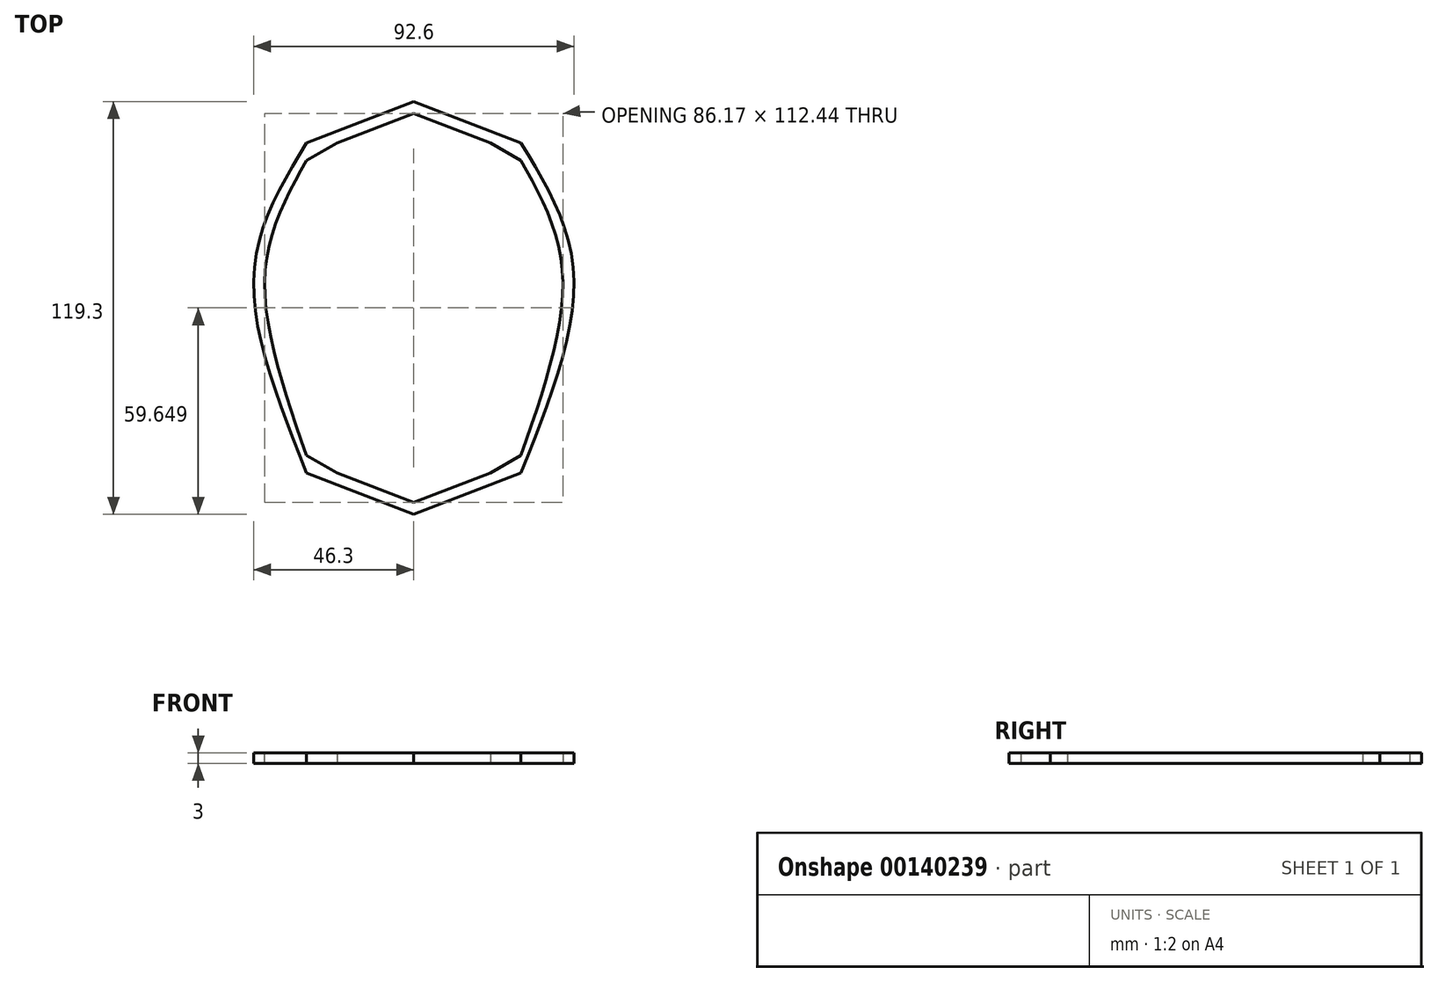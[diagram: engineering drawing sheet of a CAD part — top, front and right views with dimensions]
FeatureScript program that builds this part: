
annotation { "Feature Type Name" : "Feature", "Feature Type Description" : "" }
export const myFeature = defineFeature(function(context is Context, id is Id, definition is map)
    precondition{}
    {
        {
            var Q0;
            Q0=qCreatedBy(makeId("Top.planeOp"),FACE);
            var sketch = newSketch(context, id + "F0", { "sketchPlane" : qUnion([Q0])});
            skLineSegment(sketch, "E0", {"start": v(0, 37.5) * mm, "end": v(0, 49.5) * mm, "construction": true});
            skLineSegment(sketch, "E1", {"start": v(-31, 37.5) * mm, "end": v(0, 49.5) * mm});
            skLineSegment(sketch, "E2", {"start": v(0, 49.5) * mm, "end": v(31, 37.5) * mm});
            skLineSegment(sketch, "E3", {"start": v(0, 49.5) * mm, "end": v(0, 46.3) * mm, "construction": true});
            skLineSegment(sketch, "E4", {"start": v(0, 46.07) * mm, "end": v(-22.14, 37.5) * mm, "construction": true});
            skLineSegment(sketch, "E5.MirrorCS", {"start": v(0, 46.07) * mm, "end": v(22.14, 37.5) * mm, "construction": true});
            skLineSegment(sketch, "E6", {"start": v(0, 46.07) * mm, "end": v(22.14, 37.5) * mm});
            skLineSegment(sketch, "E7", {"start": v(0, 46.07) * mm, "end": v(-22.14, 37.5) * mm});
            skLineSegment(sketch, "E8", {"start": v(-43, 0) * mm, "end": v(-46.2, 0) * mm, "construction": true});
            skLineSegment(sketch, "E9", {"start": v(43, 0) * mm, "end": v(46.2, 0) * mm, "construction": true});
            skLineSegment(sketch, "E10", {"start": v(0, -28.4) * mm, "end": v(0, -57.8) * mm, "construction": true});
            skFitSpline(sketch, "E11", {"points": [v(-31, 37.5) * mm, v(-46.2, 0) * mm, v(-31, -57.8) * mm], "startDerivative": vector(-47.53, -78.05) * mm, "endDerivative": vector(44.54, -111.47) * mm});
            skFitSpline(sketch, "E12", {"points": [v(-31, 32.5) * mm, v(-43, 0) * mm, v(-31, -52.8) * mm], "startDerivative": vector(-37.8, -68.26) * mm, "endDerivative": vector(35.1, -101.12) * mm});
            skLineSegment(sketch, "E13", {"start": v(0, -57.8) * mm, "end": v(0, -69.8) * mm, "construction": true});
            skLineSegment(sketch, "E14", {"start": v(0, -69.8) * mm, "end": v(0, -66.37) * mm, "construction": true});
            skLineSegment(sketch, "E15", {"start": v(-22.14, -57.8) * mm, "end": v(0, -66.37) * mm});
            skLineSegment(sketch, "E16", {"start": v(0, -66.37) * mm, "end": v(22.14, -57.8) * mm});
            skLineSegment(sketch, "E17", {"start": v(-31, -57.8) * mm, "end": v(0, -69.8) * mm});
            skLineSegment(sketch, "E18", {"start": v(0, -69.8) * mm, "end": v(31, -57.8) * mm});
            skFitSpline(sketch, "E19", {"points": [v(31, 32.5) * mm, v(43, 0) * mm, v(31, -52.8) * mm], "startDerivative": vector(37.8, -68.26) * mm, "endDerivative": vector(-35.1, -101.12) * mm});
            skFitSpline(sketch, "E20", {"points": [v(31, 37.5) * mm, v(46.2, 0) * mm, v(31, -57.8) * mm], "startDerivative": vector(47.53, -78.05) * mm, "endDerivative": vector(-44.54, -111.47) * mm});
            skLineSegment(sketch, "E21", {"start": v(-31, -52.8) * mm, "end": v(-22.14, -57.8) * mm});
            skLineSegment(sketch, "E22", {"start": v(-31, 32.5) * mm, "end": v(-22.14, 37.5) * mm});
            skLineSegment(sketch, "E23", {"start": v(22.14, 37.5) * mm, "end": v(31, 32.5) * mm});
            skPoint(sketch, "E24.orphan", {"position": v(0, 43.5) * mm});
            skPoint(sketch, "E25.start.orphan", {"position": v(34.2, 37.5) * mm});
            skLineSegment(sketch, "E26", {"start": v(22.14, -57.8) * mm, "end": v(31, -52.8) * mm});
            skSolve(sketch);
        }
        {
            var Q0;
            Q0=qSketchRegion(id+"F0",true);
            extrude(context, id + "F1", {"entities" : qUnion([Q0]), "endBound" : BoundingType.SYMMETRIC, "depth" : 3 * mm});
        }
    });
